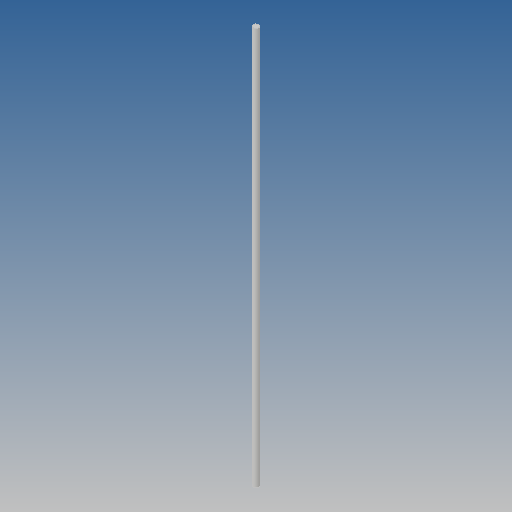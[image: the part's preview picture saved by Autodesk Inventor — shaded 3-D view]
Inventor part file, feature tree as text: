
AUTODESK INVENTOR PART (.ipt)
format: ipt  version: 2018 (Build 220112000, 112)  size: 75,264 bytes
history: native  units: mm
features: other x1, extrude x1, sketch x1
ambient origin geometry x8: Origin, YZ Plane, XZ Plane, XY Plane, X Axis, Y Axis, Z Axis, Center Point
bodies: Solid1 (feature_tree)
feature tree (3):
  other  "<userpath>\OneDrive\Objet3D\3DPrinter\Parameters.xlsx"
  extrude  "Extrusion1"  Depth=560.0mm
  sketch  "Sketch1"  dims[d0=8.0mm d1=560.0mm d2=0.0mm]
